# Revit family: Pantry Shelving
name_source: partatom
category: Generic Models
revit_build: Autodesk Revit Architecture 2012 (Build: 20110309_2315(x64)
units: mm (PartAtom-declared; Revit-internal decimal feet)

## types (17) — shared parameters
Bottom Shelf Height = 0' - 6"
Pole Height = 6' - 2"
Top Shelf Distance from Top of Pole = 0' - 8"

## per-type parameters (varying)
| type | Depth | Width |
| 48" Wide x 14" Deep | 1' - 2" | 4' - 0" |
| 36" Wide x 14" Deep | 1' - 2" | 3' - 0" |
| 42" Wide x 14" Deep | 1' - 2" | 3' - 6" |
| 60" Wide x 14" Deep | 1' - 2" | 5' - 0" |
| 72" Wide x 14" Deep | 1' - 2" | 6' - 0" |
| 36" Wide x 18" Deep | 1' - 6" | 3' - 0" |
| 42" Wide x 18" Deep | 1' - 6" | 3' - 6" |
| 48" Wide x 18" Deep | 1' - 6" | 4' - 0" |
| 60" Wide x 18" Deep | 1' - 6" | 5' - 0" |
| 54" Wide x 18" Deep | 1' - 6" | 4' - 6" |
| 72" Wide x 18" Deep | 1' - 6" | 6' - 0" |
| 36" Wide x 24" Deep | 2' - 0" | 3' - 0" |
| 42" Wide x 24" Deep | 2' - 0" | 3' - 6" |
| 48" Wide x 24" Deep | 2' - 0" | 4' - 0" |
| 54" Wide x 24" Deep | 2' - 0" | 4' - 6" |
| 60" Wide x 24" Deep | 2' - 0" | 5' - 0" |
| 72" Wide x 24" Deep | 2' - 0" | 6' - 0" |

## geometry (parser evidence)
native form markers: Sweep x1
no freeform markers — native parametric forms only
